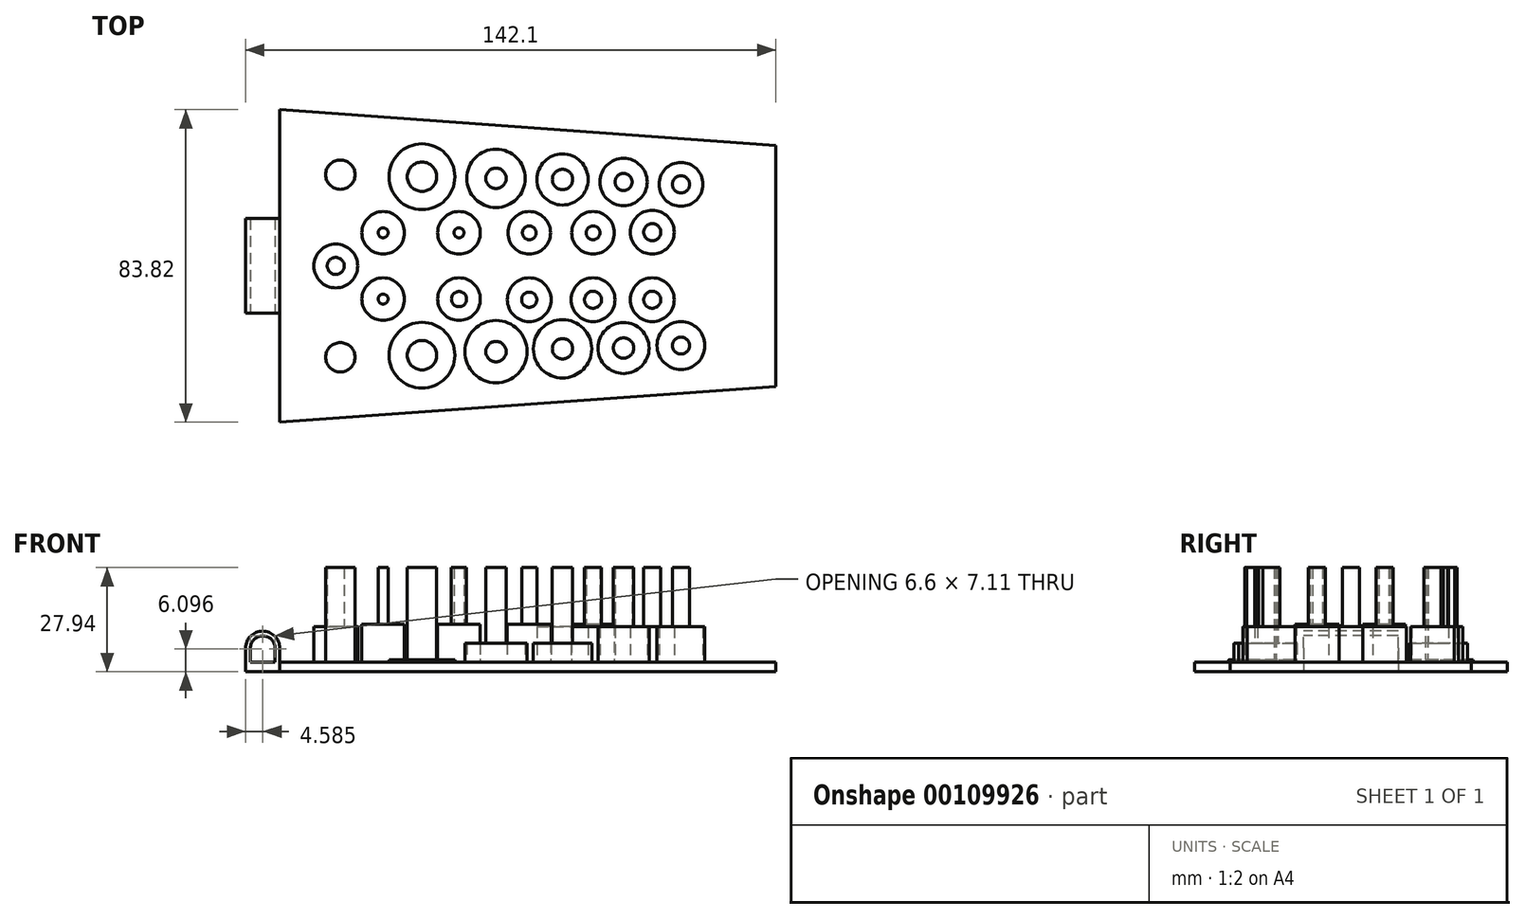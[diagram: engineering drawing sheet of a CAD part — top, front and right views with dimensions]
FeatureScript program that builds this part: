
annotation { "Feature Type Name" : "Feature", "Feature Type Description" : "" }
export const myFeature = defineFeature(function(context is Context, id is Id, definition is map)
    precondition{}
    {
        {
            var Q0;
            Q0=qCreatedBy(makeId("Top.planeOp"),FACE);
            var sketch = newSketch(context, id + "F0", { "sketchPlane" : qUnion([Q0])});
            skLineSegment(sketch, "E0", {"start": v(-71.05, 12.7) * mm, "end": v(-71.05, -12.7) * mm});
            skLineSegment(sketch, "E1", {"start": v(-61.88, -41.9) * mm, "end": v(71.05, -32.3) * mm});
            skLineSegment(sketch, "E2", {"start": v(71.05, -32.3) * mm, "end": v(71.05, 32.3) * mm});
            skLineSegment(sketch, "E3", {"start": v(71.05, 32.3) * mm, "end": v(-61.88, 41.9) * mm});
            skCircle(sketch, "E4", {"center": v(-45.65, 24.49) * mm, "radius": 9.88 * mm});
            skCircle(sketch, "E5", {"center": v(-34.18, 8.89) * mm, "radius": 5.72 * mm});
            skCircle(sketch, "E6", {"center": v(-23.77, 23.93) * mm, "radius": 8.83 * mm});
            skCircle(sketch, "E7", {"center": v(-13.85, 8.89) * mm, "radius": 5.72 * mm});
            skCircle(sketch, "E8", {"center": v(-3.94, 23.5) * mm, "radius": 7.82 * mm});
            skCircle(sketch, "E9", {"center": v(4.98, 8.89) * mm, "radius": 5.72 * mm});
            skCircle(sketch, "E10", {"center": v(13.9, 23.2) * mm, "radius": 6.85 * mm});
            skCircle(sketch, "E11", {"center": v(22.08, 8.89) * mm, "radius": 5.72 * mm});
            skCircle(sketch, "E12", {"center": v(30.26, 22.52) * mm, "radius": 6.34 * mm});
            skLineSegment(sketch, "E13", {"start": v(-34.18, 3.17) * mm, "end": v(37.95, 3.17) * mm, "construction": true});
            skCircle(sketch, "E14", {"center": v(37.95, 9.06) * mm, "radius": 5.88 * mm});
            skCircle(sketch, "E15", {"center": v(45.65, 21.88) * mm, "radius": 5.88 * mm});
            skLineSegment(sketch, "E16", {"start": v(-45.65, 34.37) * mm, "end": v(45.65, 27.76) * mm, "construction": true});
            skCircle(sketch, "E17", {"center": v(-45.65, -24.49) * mm, "radius": 9.88 * mm});
            skCircle(sketch, "E18", {"center": v(-23.77, -23.93) * mm, "radius": 8.83 * mm});
            skCircle(sketch, "E19", {"center": v(-3.94, -22.97) * mm, "radius": 8.36 * mm});
            skCircle(sketch, "E20", {"center": v(13.9, -22.22) * mm, "radius": 7.82 * mm});
            skCircle(sketch, "E21", {"center": v(30.26, -22.01) * mm, "radius": 6.85 * mm});
            skCircle(sketch, "E22", {"center": v(45.65, -21.35) * mm, "radius": 6.41 * mm});
            skLineSegment(sketch, "E23", {"start": v(-45.65, -34.37) * mm, "end": v(45.65, -27.76) * mm, "construction": true});
            skCircle(sketch, "E24", {"center": v(-34.18, -8.9) * mm, "radius": 5.72 * mm});
            skCircle(sketch, "E25", {"center": v(-13.85, -8.9) * mm, "radius": 5.72 * mm});
            skCircle(sketch, "E26", {"center": v(4.98, -9.06) * mm, "radius": 5.88 * mm});
            skCircle(sketch, "E27", {"center": v(22.08, -9.06) * mm, "radius": 5.88 * mm});
            skCircle(sketch, "E28", {"center": v(37.95, -9.06) * mm, "radius": 5.88 * mm});
            skLineSegment(sketch, "E29", {"start": v(-34.18, -3.18) * mm, "end": v(37.95, -3.18) * mm, "construction": true});
            skCircle(sketch, "E30", {"center": v(-46.88, 0) * mm, "radius": 5.88 * mm});
            skLineSegment(sketch, "E31", {"start": v(-61.88, -41.9) * mm, "end": v(-61.88, -12.7) * mm});
            skLineSegment(sketch, "E32", {"start": v(-61.88, -12.7) * mm, "end": v(-71.05, -12.7) * mm});
            skLineSegment(sketch, "E33", {"start": v(-61.88, 41.9) * mm, "end": v(-61.88, 12.7) * mm});
            skLineSegment(sketch, "E34", {"start": v(-61.88, 12.7) * mm, "end": v(-71.05, 12.7) * mm});
            skSolve(sketch);
        }
        {
            var Q0;
            Q0=makeQuery(id+"F0.imprint","IMPRINT",FACE,{"disambiguationData":[TD([[makeQuery(id+"F0.imprint","IMPRINT",EDGE,{"derivedFrom":sQuery(id+"F0.wireOp",EDGE,"E4")}),1.0]])]});
            var Q1;
            Q1=makeQuery(id+"F0.imprint","IMPRINT",FACE,{"disambiguationData":[TD([[makeQuery(id+"F0.imprint","IMPRINT",EDGE,{"derivedFrom":sQuery(id+"F0.wireOp",EDGE,"E6")}),1.0]])]});
            var Q2;
            Q2=makeQuery(id+"F0.imprint","IMPRINT",FACE,{"disambiguationData":[TD([[makeQuery(id+"F0.imprint","IMPRINT",EDGE,{"derivedFrom":sQuery(id+"F0.wireOp",EDGE,"E8")}),1.0]])]});
            var Q3;
            Q3=makeQuery(id+"F0.imprint","IMPRINT",FACE,{"disambiguationData":[TD([[makeQuery(id+"F0.imprint","IMPRINT",EDGE,{"derivedFrom":sQuery(id+"F0.wireOp",EDGE,"E10")}),1.0]])]});
            var Q4;
            Q4=makeQuery(id+"F0.imprint","IMPRINT",FACE,{"disambiguationData":[TD([[makeQuery(id+"F0.imprint","IMPRINT",EDGE,{"derivedFrom":sQuery(id+"F0.wireOp",EDGE,"E12")}),1.0]])]});
            var Q5;
            Q5=makeQuery(id+"F0.imprint","IMPRINT",FACE,{"disambiguationData":[TD([[makeQuery(id+"F0.imprint","IMPRINT",EDGE,{"derivedFrom":sQuery(id+"F0.wireOp",EDGE,"E15")}),1.0]])]});
            var Q6;
            Q6=makeQuery(id+"F0.imprint","IMPRINT",FACE,{"disambiguationData":[TD([[makeQuery(id+"F0.imprint","IMPRINT",EDGE,{"derivedFrom":sQuery(id+"F0.wireOp",EDGE,"E14")}),1.0]])]});
            var Q7;
            Q7=makeQuery(id+"F0.imprint","IMPRINT",FACE,{"disambiguationData":[TD([[makeQuery(id+"F0.imprint","IMPRINT",EDGE,{"derivedFrom":sQuery(id+"F0.wireOp",EDGE,"E11")}),1.0]])]});
            var Q8;
            Q8=makeQuery(id+"F0.imprint","IMPRINT",FACE,{"disambiguationData":[TD([[makeQuery(id+"F0.imprint","IMPRINT",EDGE,{"derivedFrom":sQuery(id+"F0.wireOp",EDGE,"E0")}),1.0]])]});
            var Q9;
            Q9=makeQuery(id+"F0.imprint","IMPRINT",FACE,{"disambiguationData":[TD([[makeQuery(id+"F0.imprint","IMPRINT",EDGE,{"derivedFrom":sQuery(id+"F0.wireOp",EDGE,"E9")}),1.0]])]});
            var Q10;
            Q10=makeQuery(id+"F0.imprint","IMPRINT",FACE,{"disambiguationData":[TD([[makeQuery(id+"F0.imprint","IMPRINT",EDGE,{"derivedFrom":sQuery(id+"F0.wireOp",EDGE,"E7")}),1.0]])]});
            var Q11;
            Q11=makeQuery(id+"F0.imprint","IMPRINT",FACE,{"disambiguationData":[TD([[makeQuery(id+"F0.imprint","IMPRINT",EDGE,{"derivedFrom":sQuery(id+"F0.wireOp",EDGE,"E5")}),1.0]])]});
            var Q12;
            Q12=makeQuery(id+"F0.imprint","IMPRINT",FACE,{"disambiguationData":[TD([[makeQuery(id+"F0.imprint","IMPRINT",EDGE,{"derivedFrom":sQuery(id+"F0.wireOp",EDGE,"E30")}),1.0]])]});
            var Q13;
            Q13=makeQuery(id+"F0.imprint","IMPRINT",FACE,{"disambiguationData":[TD([[makeQuery(id+"F0.imprint","IMPRINT",EDGE,{"derivedFrom":sQuery(id+"F0.wireOp",EDGE,"E24")}),1.0]])]});
            var Q14;
            Q14=makeQuery(id+"F0.imprint","IMPRINT",FACE,{"disambiguationData":[TD([[makeQuery(id+"F0.imprint","IMPRINT",EDGE,{"derivedFrom":sQuery(id+"F0.wireOp",EDGE,"E25")}),1.0]])]});
            var Q15;
            Q15=makeQuery(id+"F0.imprint","IMPRINT",FACE,{"disambiguationData":[TD([[makeQuery(id+"F0.imprint","IMPRINT",EDGE,{"derivedFrom":sQuery(id+"F0.wireOp",EDGE,"E26")}),1.0]])]});
            var Q16;
            Q16=makeQuery(id+"F0.imprint","IMPRINT",FACE,{"disambiguationData":[TD([[makeQuery(id+"F0.imprint","IMPRINT",EDGE,{"derivedFrom":sQuery(id+"F0.wireOp",EDGE,"E27")}),1.0]])]});
            var Q17;
            Q17=makeQuery(id+"F0.imprint","IMPRINT",FACE,{"disambiguationData":[TD([[makeQuery(id+"F0.imprint","IMPRINT",EDGE,{"derivedFrom":sQuery(id+"F0.wireOp",EDGE,"E28")}),1.0]])]});
            var Q18;
            Q18=makeQuery(id+"F0.imprint","IMPRINT",FACE,{"disambiguationData":[TD([[makeQuery(id+"F0.imprint","IMPRINT",EDGE,{"derivedFrom":sQuery(id+"F0.wireOp",EDGE,"E22")}),1.0]])]});
            var Q19;
            Q19=makeQuery(id+"F0.imprint","IMPRINT",FACE,{"disambiguationData":[TD([[makeQuery(id+"F0.imprint","IMPRINT",EDGE,{"derivedFrom":sQuery(id+"F0.wireOp",EDGE,"E21")}),1.0]])]});
            var Q20;
            Q20=makeQuery(id+"F0.imprint","IMPRINT",FACE,{"disambiguationData":[TD([[makeQuery(id+"F0.imprint","IMPRINT",EDGE,{"derivedFrom":sQuery(id+"F0.wireOp",EDGE,"E20")}),1.0]])]});
            var Q21;
            Q21=makeQuery(id+"F0.imprint","IMPRINT",FACE,{"disambiguationData":[TD([[makeQuery(id+"F0.imprint","IMPRINT",EDGE,{"derivedFrom":sQuery(id+"F0.wireOp",EDGE,"E19")}),1.0]])]});
            var Q22;
            Q22=makeQuery(id+"F0.imprint","IMPRINT",FACE,{"disambiguationData":[TD([[makeQuery(id+"F0.imprint","IMPRINT",EDGE,{"derivedFrom":sQuery(id+"F0.wireOp",EDGE,"E18")}),1.0]])]});
            var Q23;
            Q23=makeQuery(id+"F0.imprint","IMPRINT",FACE,{"disambiguationData":[TD([[makeQuery(id+"F0.imprint","IMPRINT",EDGE,{"derivedFrom":sQuery(id+"F0.wireOp",EDGE,"E17")}),1.0]])]});
            extrude(context, id + "F1", {"entities" : qUnion([Q0, Q1, Q2, Q3, Q4, Q5, Q6, Q7, Q8, Q9, Q10, Q11, Q12, Q13, Q14, Q15, Q16, Q17, Q18, Q19, Q20, Q21, Q22, Q23]), "depth" : 2.54 * mm});
        }
        {
            var Q0;
            Q0=makeQuery(id+"F0.imprint","IMPRINT",FACE,{"disambiguationData":[TD([[makeQuery(id+"F0.imprint","IMPRINT",EDGE,{"derivedFrom":sQuery(id+"F0.wireOp",EDGE,"E6")}),1.0]])]});
            var Q1;
            Q1=makeQuery(id+"F0.imprint","IMPRINT",FACE,{"disambiguationData":[TD([[makeQuery(id+"F0.imprint","IMPRINT",EDGE,{"derivedFrom":sQuery(id+"F0.wireOp",EDGE,"E18")}),1.0]])]});
            extrude(context, id + "F2", {"entities" : qUnion([Q0, Q1]), "operationType" : NewBodyOperationType.ADD, "depth" : 3.17 * mm});
        }
        {
            var Q0;
            Q0=makeQuery(id+"F0.imprint","IMPRINT",FACE,{"disambiguationData":[TD([[makeQuery(id+"F0.imprint","IMPRINT",EDGE,{"derivedFrom":sQuery(id+"F0.wireOp",EDGE,"E8")}),1.0]])]});
            var Q1;
            Q1=makeQuery(id+"F0.imprint","IMPRINT",FACE,{"disambiguationData":[TD([[makeQuery(id+"F0.imprint","IMPRINT",EDGE,{"derivedFrom":sQuery(id+"F0.wireOp",EDGE,"E19")}),1.0]])]});
            var Q2;
            Q2=makeQuery(id+"F0.imprint","IMPRINT",FACE,{"disambiguationData":[TD([[makeQuery(id+"F0.imprint","IMPRINT",EDGE,{"derivedFrom":sQuery(id+"F0.wireOp",EDGE,"E20")}),1.0]])]});
            extrude(context, id + "F3", {"entities" : qUnion([Q0, Q1, Q2]), "operationType" : NewBodyOperationType.ADD, "depth" : 7.62 * mm});
        }
        {
            var Q0;
            Q0=makeQuery(id+"F0.imprint","IMPRINT",FACE,{"disambiguationData":[TD([[makeQuery(id+"F0.imprint","IMPRINT",EDGE,{"derivedFrom":sQuery(id+"F0.wireOp",EDGE,"E10")}),1.0]])]});
            var Q1;
            Q1=makeQuery(id+"F0.imprint","IMPRINT",FACE,{"disambiguationData":[TD([[makeQuery(id+"F0.imprint","IMPRINT",EDGE,{"derivedFrom":sQuery(id+"F0.wireOp",EDGE,"E12")}),1.0]])]});
            var Q2;
            Q2=makeQuery(id+"F0.imprint","IMPRINT",FACE,{"disambiguationData":[TD([[makeQuery(id+"F0.imprint","IMPRINT",EDGE,{"derivedFrom":sQuery(id+"F0.wireOp",EDGE,"E15")}),1.0]])]});
            var Q3;
            Q3=makeQuery(id+"F0.imprint","IMPRINT",FACE,{"disambiguationData":[TD([[makeQuery(id+"F0.imprint","IMPRINT",EDGE,{"derivedFrom":sQuery(id+"F0.wireOp",EDGE,"E21")}),1.0]])]});
            var Q4;
            Q4=makeQuery(id+"F0.imprint","IMPRINT",FACE,{"disambiguationData":[TD([[makeQuery(id+"F0.imprint","IMPRINT",EDGE,{"derivedFrom":sQuery(id+"F0.wireOp",EDGE,"E22")}),1.0]])]});
            var Q5;
            Q5=makeQuery(id+"F0.imprint","IMPRINT",FACE,{"disambiguationData":[TD([[makeQuery(id+"F0.imprint","IMPRINT",EDGE,{"derivedFrom":sQuery(id+"F0.wireOp",EDGE,"E28")}),1.0]])]});
            var Q6;
            Q6=makeQuery(id+"F0.imprint","IMPRINT",FACE,{"disambiguationData":[TD([[makeQuery(id+"F0.imprint","IMPRINT",EDGE,{"derivedFrom":sQuery(id+"F0.wireOp",EDGE,"E27")}),1.0]])]});
            var Q7;
            Q7=makeQuery(id+"F0.imprint","IMPRINT",FACE,{"disambiguationData":[TD([[makeQuery(id+"F0.imprint","IMPRINT",EDGE,{"derivedFrom":sQuery(id+"F0.wireOp",EDGE,"E14")}),1.0]])]});
            var Q8;
            Q8=makeQuery(id+"F0.imprint","IMPRINT",FACE,{"disambiguationData":[TD([[makeQuery(id+"F0.imprint","IMPRINT",EDGE,{"derivedFrom":sQuery(id+"F0.wireOp",EDGE,"E30")}),1.0]])]});
            extrude(context, id + "F4", {"entities" : qUnion([Q0, Q1, Q2, Q3, Q4, Q5, Q6, Q7, Q8]), "operationType" : NewBodyOperationType.ADD, "depth" : 12.06 * mm});
        }
        {
            var Q0;
            Q0=makeQuery(id+"F0.imprint","IMPRINT",FACE,{"disambiguationData":[TD([[makeQuery(id+"F0.imprint","IMPRINT",EDGE,{"derivedFrom":sQuery(id+"F0.wireOp",EDGE,"E7")}),1.0]])]});
            var Q1;
            Q1=makeQuery(id+"F0.imprint","IMPRINT",FACE,{"disambiguationData":[TD([[makeQuery(id+"F0.imprint","IMPRINT",EDGE,{"derivedFrom":sQuery(id+"F0.wireOp",EDGE,"E9")}),1.0]])]});
            var Q2;
            Q2=makeQuery(id+"F0.imprint","IMPRINT",FACE,{"disambiguationData":[TD([[makeQuery(id+"F0.imprint","IMPRINT",EDGE,{"derivedFrom":sQuery(id+"F0.wireOp",EDGE,"E11")}),1.0]])]});
            var Q3;
            Q3=makeQuery(id+"F0.imprint","IMPRINT",FACE,{"disambiguationData":[TD([[makeQuery(id+"F0.imprint","IMPRINT",EDGE,{"derivedFrom":sQuery(id+"F0.wireOp",EDGE,"E26")}),1.0]])]});
            var Q4;
            Q4=makeQuery(id+"F0.imprint","IMPRINT",FACE,{"disambiguationData":[TD([[makeQuery(id+"F0.imprint","IMPRINT",EDGE,{"derivedFrom":sQuery(id+"F0.wireOp",EDGE,"E25")}),1.0]])]});
            var Q5;
            Q5=makeQuery(id+"F0.imprint","IMPRINT",FACE,{"disambiguationData":[TD([[makeQuery(id+"F0.imprint","IMPRINT",EDGE,{"derivedFrom":sQuery(id+"F0.wireOp",EDGE,"E24")}),1.0]])]});
            var Q6;
            Q6=makeQuery(id+"F0.imprint","IMPRINT",FACE,{"disambiguationData":[TD([[makeQuery(id+"F0.imprint","IMPRINT",EDGE,{"derivedFrom":sQuery(id+"F0.wireOp",EDGE,"E5")}),1.0]])]});
            var Q7;
            Q7=sQuery(id+"F0.wireOp",EDGE,"E12");
            extrude(context, id + "F5", {"entities" : qUnion([Q0, Q1, Q2, Q3, Q4, Q5, Q6]), "operationType" : NewBodyOperationType.ADD, "surfaceEntities" : qUnion([Q7]), "depth" : 12.7 * mm});
        }
        {
            var Q0;
            Q0=makeQuery(id+"F1.opExtrude","CAP_FACE",FACE,{"disambiguationData":[OSD([sQuery(id+"F0.wireOp",EDGE,"E0"),sQuery(id+"F0.wireOp",EDGE,"E1"),sQuery(id+"F0.wireOp",EDGE,"E2"),sQuery(id+"F0.wireOp",EDGE,"E3")])],"isStart":false});
            var sketch = newSketch(context, id + "F6", { "sketchPlane" : qUnion([Q0])});
            skCircle(sketch, "E35", {"center": v(-45.65, 24.49) * mm, "radius": 3.94 * mm});
            skCircle(sketch, "E36", {"center": v(-23.77, 23.93) * mm, "radius": 3.94 * mm});
            skCircle(sketch, "E37", {"center": v(-3.94, 23.5) * mm, "radius": 2.73 * mm});
            skCircle(sketch, "E38", {"center": v(13.9, 23.2) * mm, "radius": 2.73 * mm});
            skCircle(sketch, "E39", {"center": v(30.26, 22.52) * mm, "radius": 2.29 * mm});
            skCircle(sketch, "E40", {"center": v(45.65, 21.88) * mm, "radius": 2.29 * mm});
            skCircle(sketch, "E41", {"center": v(37.95, 9.06) * mm, "radius": 2.29 * mm});
            skCircle(sketch, "E42", {"center": v(22.08, 8.9) * mm, "radius": 1.84 * mm});
            skCircle(sketch, "E43", {"center": v(4.98, 8.9) * mm, "radius": 1.84 * mm});
            skCircle(sketch, "E44", {"center": v(-13.85, 8.89) * mm, "radius": 1.33 * mm});
            skCircle(sketch, "E45", {"center": v(-34.18, 8.89) * mm, "radius": 1.33 * mm});
            skCircle(sketch, "E46", {"center": v(-45.65, -24.49) * mm, "radius": 3.94 * mm});
            skCircle(sketch, "E47", {"center": v(-23.77, -23.93) * mm, "radius": 3.94 * mm});
            skCircle(sketch, "E48", {"center": v(-3.94, -22.97) * mm, "radius": 2.73 * mm});
            skCircle(sketch, "E49", {"center": v(13.9, -22.22) * mm, "radius": 2.73 * mm});
            skCircle(sketch, "E50", {"center": v(30.26, -22.01) * mm, "radius": 2.73 * mm});
            skCircle(sketch, "E51", {"center": v(45.65, -21.35) * mm, "radius": 2.29 * mm});
            skCircle(sketch, "E52", {"center": v(37.95, -9.06) * mm, "radius": 2.29 * mm});
            skCircle(sketch, "E53", {"center": v(22.08, -9.06) * mm, "radius": 2.29 * mm});
            skCircle(sketch, "E54", {"center": v(4.98, -9.06) * mm, "radius": 2.03 * mm});
            skCircle(sketch, "E55", {"center": v(-13.85, -8.89) * mm, "radius": 2.03 * mm});
            skCircle(sketch, "E56", {"center": v(-34.18, -8.89) * mm, "radius": 1.33 * mm});
            skCircle(sketch, "E57", {"center": v(-46.88, 0) * mm, "radius": 2.29 * mm});
            skSolve(sketch);
        }
        {
            var Q0;
            Q0 = qSketchRegion(id + "F6", true);
            extrude(context, id + "F7", {"entities" : qUnion([Q0]), "operationType" : NewBodyOperationType.ADD, "depth" : 25.4 * mm});
        }
        {
            var Q0;
            Q0=makeQuery(id+"F1.opExtrude","SWEPT_FACE",FACE,{"disambiguationData":[OSD([sQuery(id+"F0.wireOp",EDGE,"E32")])]});
            var sketch = newSketch(context, id + "F8", { "sketchPlane" : qUnion([Q0])});
            skLineSegment(sketch, "E58", {"start": v(-71.05, 2.54) * mm, "end": v(-71.05, 6.35) * mm});
            skArc(sketch, "E59", {"start": v(-61.88, 6.35) * mm, "mid": v(-66.47, 10.93) * mm, "end": v(-71.05, 6.35) * mm});
            skLineSegment(sketch, "E60", {"start": v(-61.88, 6.35) * mm, "end": v(-61.88, 2.54) * mm});
            skLineSegment(sketch, "E61.0", {"start": v(-69.77, 2.54) * mm, "end": v(-69.77, 6.35) * mm});
            skArc(sketch, "E61.1", {"start": v(-63.16, 6.35) * mm, "mid": v(-66.47, 9.65) * mm, "end": v(-69.77, 6.35) * mm});
            skLineSegment(sketch, "E61.2", {"start": v(-63.16, 6.35) * mm, "end": v(-63.16, 2.54) * mm});
            skLineSegment(sketch, "E62", {"start": v(-63.16, 2.54) * mm, "end": v(-61.88, 2.54) * mm});
            skLineSegment(sketch, "E63", {"start": v(-69.77, 2.54) * mm, "end": v(-71.05, 2.54) * mm});
            skSolve(sketch);
        }
        {
            var Q0;
            Q0 = qSketchRegion(id + "F8", true);
            var Q1;
            Q1=makeQuery(id+"F1.opExtrude","SWEPT_FACE",FACE,{"disambiguationData":[OSD([sQuery(id+"F0.wireOp",EDGE,"E34")])]});
            extrude(context, id + "F9", {"entities" : qUnion([Q0]), "operationType" : NewBodyOperationType.ADD, "endBound" : BoundingType.UP_TO_SURFACE, "oppositeDirection" : true, "endBoundEntityFace" : qUnion([Q1]), "depth" : 25.4 * mm});
        }
    });
